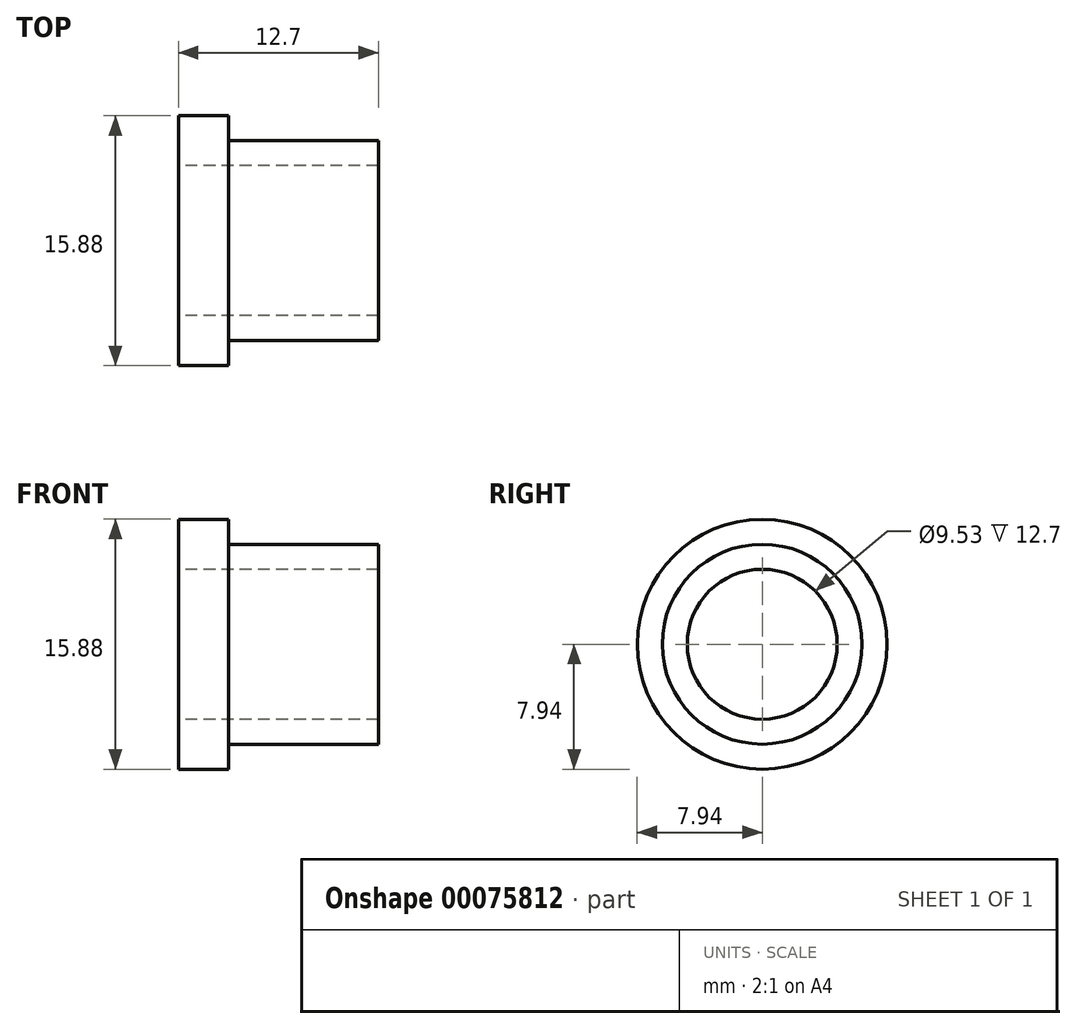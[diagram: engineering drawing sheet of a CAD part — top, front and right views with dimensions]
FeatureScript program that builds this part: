
annotation { "Feature Type Name" : "Feature", "Feature Type Description" : "" }
export const myFeature = defineFeature(function(context is Context, id is Id, definition is map)
    precondition{}
    {
        {
            var Q0;
            Q0=qCreatedBy(makeId("Front.planeOp"),FACE);
            var sketch = newSketch(context, id + "F0", { "sketchPlane" : qUnion([Q0])});
            skLineSegment(sketch, "E0", {"start": v(0, 7.94) * mm, "end": v(0, 4.76) * mm});
            skLineSegment(sketch, "E1", {"start": v(0, 4.76) * mm, "end": v(12.7, 4.76) * mm});
            skLineSegment(sketch, "E2", {"start": v(12.7, 4.76) * mm, "end": v(12.7, 6.35) * mm});
            skLineSegment(sketch, "E3", {"start": v(12.7, 6.35) * mm, "end": v(3.18, 6.35) * mm});
            skLineSegment(sketch, "E4", {"start": v(3.18, 6.35) * mm, "end": v(3.18, 7.94) * mm});
            skLineSegment(sketch, "E5", {"start": v(3.18, 7.94) * mm, "end": v(0, 7.94) * mm});
            skLineSegment(sketch, "E6", {"start": v(0, 0) * mm, "end": v(21.96, 0) * mm, "construction": true});
            skSolve(sketch);
        }
        {
            var Q0;
            Q0 = qSketchRegion(id + "F0", true);
            var Q1;
            Q1=sQuery(id+"F0.wireOp",EDGE,"E6");
            revolve(context, id + "F1", {"entities" : qUnion([Q0]), "axis" : qUnion([Q1]), "revolveType" : RevolveType.FULL});
        }
    });
